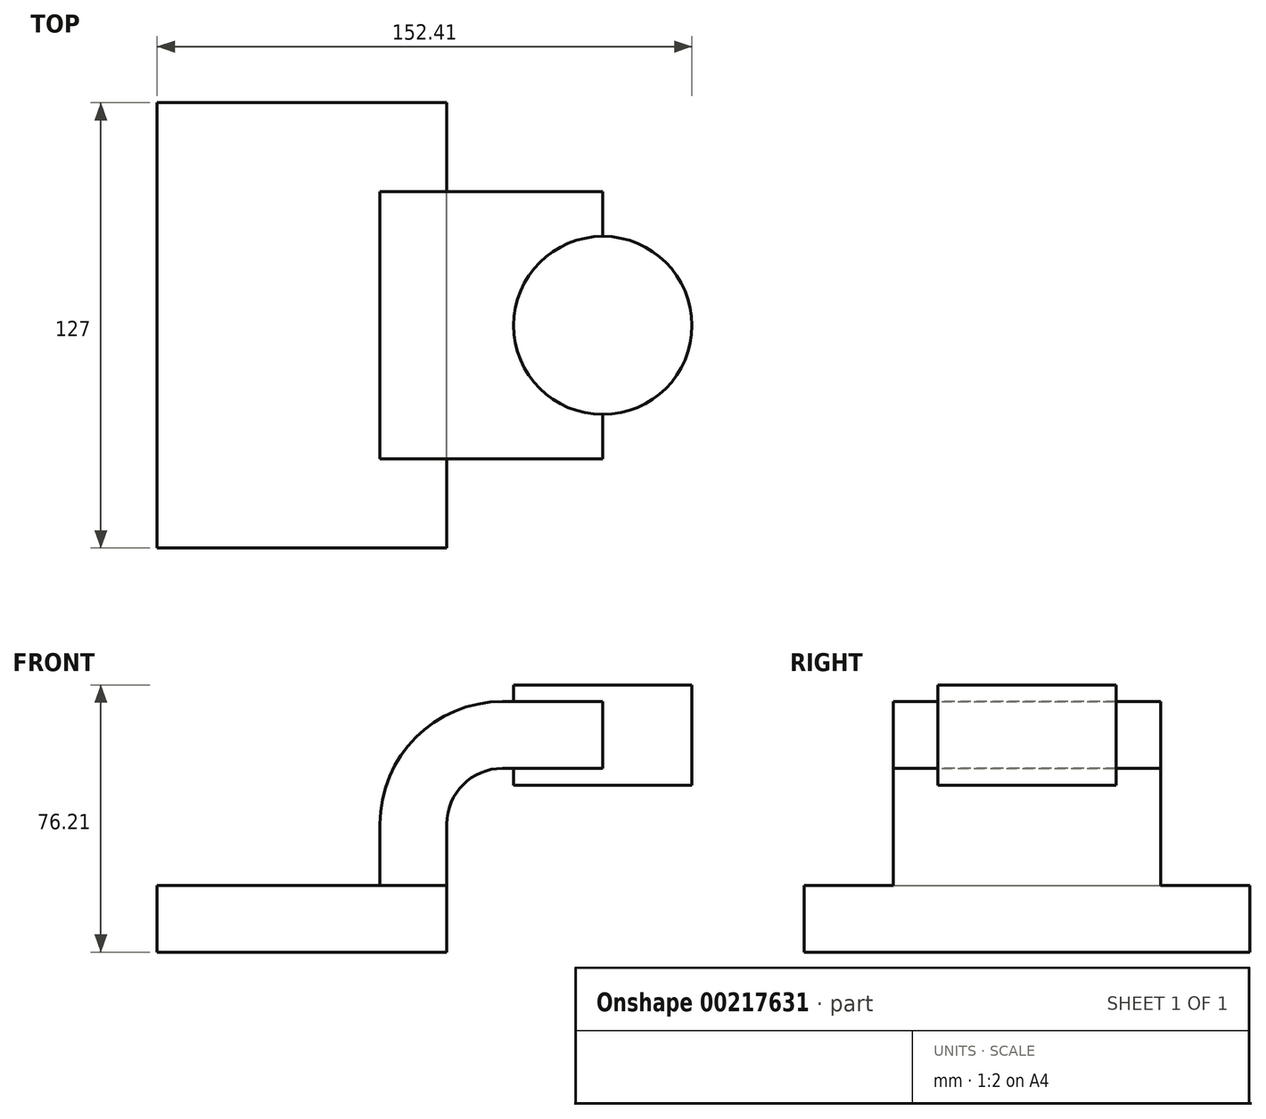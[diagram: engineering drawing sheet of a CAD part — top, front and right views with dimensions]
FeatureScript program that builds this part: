
annotation { "Feature Type Name" : "Feature", "Feature Type Description" : "" }
export const myFeature = defineFeature(function(context is Context, id is Id, definition is map)
    precondition{}
    {
        {
            var Q0;
            Q0=qCreatedBy(makeId("Front.planeOp"),FACE);
            var sketch = newSketch(context, id + "F0", { "sketchPlane" : qUnion([Q0])});
            skLineSegment(sketch, "E0.bottom", {"start": v(-41.27, -9.53) * mm, "end": v(41.28, -9.53) * mm});
            skLineSegment(sketch, "E0.top", {"start": v(-41.28, 9.52) * mm, "end": v(41.28, 9.52) * mm});
            skLineSegment(sketch, "E0.left", {"start": v(-41.28, -9.53) * mm, "end": v(-41.28, 9.52) * mm});
            skLineSegment(sketch, "E0.right", {"start": v(41.28, -9.53) * mm, "end": v(41.28, 9.52) * mm});
            skPoint(sketch, "E0.middle", {"position": v(0, 0) * mm});
            skLineSegment(sketch, "E1.bottom", {"start": v(111.13, 38.1) * mm, "end": v(60.33, 38.1) * mm});
            skLineSegment(sketch, "E1.top", {"start": v(111.12, 66.68) * mm, "end": v(60.32, 66.68) * mm});
            skLineSegment(sketch, "E1.left", {"start": v(111.13, 38.1) * mm, "end": v(111.12, 66.68) * mm});
            skLineSegment(sketch, "E1.right", {"start": v(60.33, 38.1) * mm, "end": v(60.32, 66.68) * mm});
            skPoint(sketch, "E1.middle", {"position": v(85.72, 52.39) * mm});
            skLineSegment(sketch, "E2", {"start": v(41.27, 9.52) * mm, "end": v(41.27, 27) * mm});
            skArc(sketch, "E3", {"start": v(41.27, 27) * mm, "mid": v(45.92, 38.23) * mm, "end": v(57.15, 42.88) * mm});
            skLineSegment(sketch, "E4", {"start": v(57.15, 42.88) * mm, "end": v(85.72, 42.88) * mm});
            skLineSegment(sketch, "E5.0", {"start": v(57.15, 61.93) * mm, "end": v(85.72, 61.93) * mm});
            skArc(sketch, "E5.1", {"start": v(22.23, 27) * mm, "mid": v(32.45, 51.7) * mm, "end": v(57.15, 61.93) * mm});
            skLineSegment(sketch, "E5.2", {"start": v(22.22, 9.52) * mm, "end": v(22.22, 27) * mm});
            skLineSegment(sketch, "E6", {"start": v(85.72, 61.93) * mm, "end": v(85.72, 42.88) * mm});
            skLineSegment(sketch, "E7", {"start": v(85.72, 61.93) * mm, "end": v(85.72, 66.68) * mm});
            skFitSpline(sketch, "E8", {"points": [v(-41.27, 9.52) * mm, v(57.15, 61.93) * mm], "startDerivative": vector(66.02, 116.9) * mm, "endDerivative": vector(144.5, -47.54) * mm});
            skLineSegment(sketch, "E9", {"start": v(85.72, 42.88) * mm, "end": v(85.72, 38.1) * mm});
            skSolve(sketch);
        }
        {
            var Q0;
            Q0=makeQuery(id+"F0.imprint","IMPRINT",FACE,{"disambiguationData":[TD([[makeQuery(id+"F0.imprint","IMPRINT",EDGE,{"derivedFrom":sQuery(id+"F0.wireOp",EDGE,"E0.bottom")}),1.0]])]});
            extrude(context, id + "F1", {"entities" : qUnion([Q0]), "endBound" : BoundingType.SYMMETRIC, "depth" : 127 * mm});
        }
        {
            var Q0;
            Q0=makeQuery(id+"F0.imprint","IMPRINT",FACE,{"disambiguationData":[TD([[makeQuery(id+"F0.imprint","IMPRINT",EDGE,{"derivedFrom":sQuery(id+"F0.wireOp",EDGE,"E5.1")}),1.0]])]});
            extrude(context, id + "F2", {"entities" : qUnion([Q0]), "operationType" : NewBodyOperationType.ADD, "endBound" : BoundingType.SYMMETRIC, "depth" : 15.88 * mm});
        }
        {
            var Q0;
            {var subQ1=sQuery(id+"F0.wireOp",EDGE,"E2");Q0=makeQuery(id+"F0.imprint","IMPRINT",FACE,{"disambiguationData":[TD([[makeQuery(id+"F0.imprint","IMPRINT",EDGE,{"derivedFrom":subQ1}),1.0]])]});}
            var Q1;
            {var subQ5=sQuery(id+"F0.wireOp",EDGE,"E6");Q1=makeQuery(id+"F0.imprint","IMPRINT",FACE,{"disambiguationData":[TD([[makeQuery(id+"F0.imprint","IMPRINT",EDGE,{"derivedFrom":subQ5}),-1.0]])]});}
            extrude(context, id + "F3", {"entities" : qUnion([Q0, Q1]), "operationType" : NewBodyOperationType.ADD, "endBound" : BoundingType.SYMMETRIC, "depth" : 76.2 * mm});
        }
        {
            var Q0;
            {var subQ0=sQuery(id+"F0.wireOp",EDGE,"E1.left");Q0=makeQuery(id+"F0.imprint","IMPRINT",FACE,{"disambiguationData":[TD([[makeQuery(id+"F0.imprint","IMPRINT",EDGE,{"derivedFrom":subQ0}),1.0]])]});}
            var Q1;
            Q1=sQuery(id+"F0.wireOp",EDGE,"E6");
            revolve(context, id + "F4", {"operationType" : NewBodyOperationType.ADD, "entities" : qUnion([Q0]), "axis" : qUnion([Q1]), "revolveType" : RevolveType.FULL});
        }
    });
